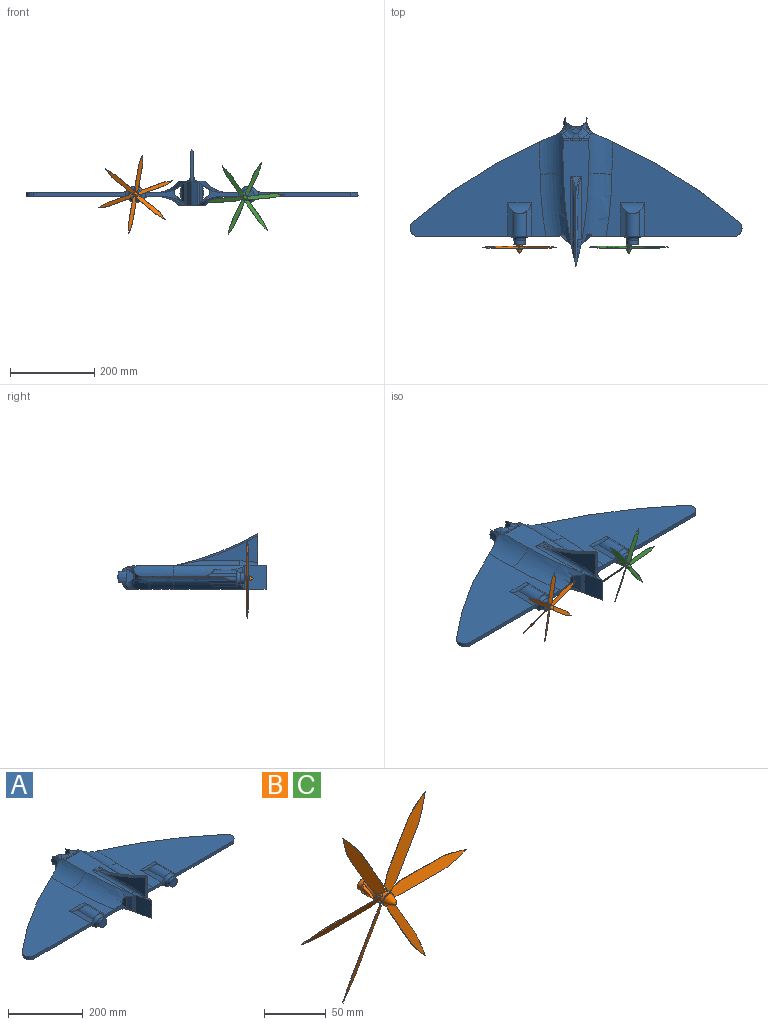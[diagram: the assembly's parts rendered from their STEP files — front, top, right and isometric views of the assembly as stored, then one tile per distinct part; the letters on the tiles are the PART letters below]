
ASSEMBLY  parts=3 mates=1
PART A: 103 faces, bbox 833.9x447.9x145.3 mm
  f0: plane 77.06x24.78mm, normal (0,-1,0), area 855.7mm2, adj f10,f21,f22,f28,f34,f40,f42,f43
  f1: plane 221.43x16.25mm, normal (0,-1,0), area 2215.1mm2, adj f2,f3,f14,f93,f95,f101
  f2: plane 321.92x225.03mm, normal (0,0,1), area 38652.2mm2, adj f1,f8,f12,f14,f31,f32,f91,f95
  f3: plane 323.52x206.51mm, normal (0,0,-1), area 32981mm2, adj f1,f8,f13,f14,f25,f26,f92,f93
  f4: plane 1.52x1.01mm, normal (0,0.71,-0.71), area 1mm2, adj f60,f77,f78
  f5: plane 19.73x12.89mm, normal (0,0.38,0.92), area 124.3mm2, adj f31,f63,f66,f72
  f6: plane 19.9x10.06mm, normal (0,0,1), area 101.6mm2, adj f15,f16,f44
  f7: plane 138.61x64.57mm, normal (-1,0,0), area 3823.6mm2, adj f44,f51,f52,f53
  f8: plane 77.03x24.74mm, normal (0,-1,0), area 855.7mm2, adj f2,f3,f11,f25,f32,f36,f37,f38
  f9: cylinder r=30mm len=39.86mm, axis (0,0,-1), area 421.5mm2, adj f12,f27,f31,f36,f37,f38,f63,f77
  f10: plane 57.68x24.14mm, normal (-0.63,-0.77,0), area 445.5mm2, adj f0,f16,f28,f34,f43,f57
  f11: plane 57.68x24.14mm, normal (0.63,-0.77,0), area 445.5mm2, adj f8,f15,f25,f32,f38,f58
  f12: cylinder r=1216.17mm len=343.76mm, axis (0,0,-1), area 1468.3mm2, adj f2,f9,f13,f14,f27,f31
  f13: torus R=1196.91mm, axis (0,0,-1), area 7777.9mm2, adj f3,f12,f14,f27
  f14: cylinder r=20.44mm len=31.58mm, axis (0,0,-1), area 312.3mm2, adj f1,f2,f3,f12,f13
  f15: cylinder r=891.18mm len=57mm, axis (0,0,1), area 2976.1mm2, adj f6,f11,f16,f17,f49,f50
  f16: cylinder r=891.18mm len=57mm, axis (0,0,1), area 2976.1mm2, adj f6,f10,f15,f17,f51
  f17: plane 330.75x64.66mm, normal (0,0,-1), area 14853.2mm2, adj f15,f16,f25,f26,f27,f28,f29,f30
  f18: plane 237.13x62.73mm, normal (0,0,1), area 8255mm2, adj f31,f32,f33,f34,f47,f48,f52,f55
  f19: cylinder r=20.44mm len=31.58mm, axis (0,0,-1), area 312.3mm2, adj f20,f21,f22,f23,f24
  f20: torus R=1196.91mm, axis (0,0,-1), area 7777.8mm2, adj f19,f21,f23,f30
  f21: plane 323.52x206.51mm, normal (0,0,-1), area 32981mm2, adj f0,f19,f20,f24,f28,f29,f83,f85
  f22: plane 321.92x225.03mm, normal (0,0,1), area 38652.2mm2, adj f0,f19,f23,f24,f33,f34,f84,f87
  f23: cylinder r=1216.17mm len=343.76mm, axis (0,0,-1), area 1468.3mm2, adj f19,f20,f22,f30,f33,f35
  f24: plane 221.43x16.25mm, normal (0,-1,0), area 2215.1mm2, adj f19,f21,f22,f86,f88,f102
  f25: torus R=940.17mm, axis (0,0,1), area 8346.4mm2, adj f3,f8,f11,f17,f26
  f26: torus R=810.61mm, axis (0,0,1), area 3113.6mm2, adj f3,f17,f25,f27
  f27: bspline ~70.07x54.57mm, area 1883.4mm2, adj f9,f12,f13,f17,f26,f77,f78
  f28: torus R=940.17mm, axis (0,0,1), area 8346.4mm2, adj f0,f10,f17,f21,f29
  f29: torus R=810.61mm, axis (0,0,1), area 3113.6mm2, adj f17,f21,f28,f30
  f30: bspline ~76.88x55.79mm, area 1883.5mm2, adj f17,f20,f23,f29,f35,f76,f80
  f31: torus R=816.85mm, axis (0,0,1), area 5583.6mm2, adj f2,f5,f9,f12,f18,f32,f63,f72
  f32: torus R=946.41mm, axis (0,0,1), area 9600.6mm2, adj f2,f8,f11,f18,f31,f36,f39,f49
  f33: torus R=816.85mm, axis (0,0,1), area 5583.6mm2, adj f18,f22,f23,f34,f35,f62,f64,f70
  f34: torus R=946.41mm, axis (0,0,1), area 9600.6mm2, adj f0,f10,f18,f22,f33,f41,f42,f51
  f35: cylinder r=30mm len=39.86mm, axis (0,0,1), area 421.5mm2, adj f23,f30,f33,f40,f42,f43,f64,f76
  f36: plane 256.61x17.38mm, normal (-0.57,0,-0.82), area 4867.7mm2, adj f8,f9,f32,f37,f39,f63,f65
  f37: plane 244.33x11.93mm, normal (-1,0,0), area 2914.8mm2, adj f8,f9,f36,f38
  f38: plane 285.27x26.63mm, normal (-0.62,0,0.79), area 5313.6mm2, adj f8,f9,f11,f37,f39,f58,f77
  f39: plane 286.48x42.71mm, normal (1,0,0), area 9851.4mm2, adj f32,f36,f38,f58,f59,f60,f65,f77
  f40: plane 244.33x11.93mm, normal (1,0,0), area 2914.8mm2, adj f0,f35,f42,f43
  f41: plane 286.48x42.71mm, normal (-1,0,0), area 9851.4mm2, adj f34,f42,f43,f57,f60,f61,f69,f76
  f42: plane 256.6x17.37mm, normal (0.57,0,-0.82), area 4867.7mm2, adj f0,f34,f35,f40,f41,f64,f69
  f43: plane 285.27x26.63mm, normal (0.62,0,0.79), area 5313.6mm2, adj f0,f10,f35,f40,f41,f57,f76
  f44: plane 74.53x10.63mm, normal (0,-1,0), area 543.5mm2, adj f6,f7,f45,f50,f51,f53,f54
  f45: plane 64.37x26.26mm, normal (1,-0.02,0), area 1436.2mm2, adj f44,f46,f49,f50,f54
  f46: plane 112.37x46.21mm, normal (1,0,0), area 2390.5mm2, adj f45,f48,f49,f54
  f47: cylinder r=820.16mm len=34.77mm, axis (-1,0,0), area 430.9mm2, adj f18,f55,f56
  f48: cylinder r=10mm len=148.7mm, axis (0,1,0), area 1925.9mm2, adj f18,f46,f49,f56
  f49: bspline ~28.84x11.57mm, area 220.2mm2, adj f15,f32,f45,f46,f48,f50
  f50: bspline ~35.02x9.75mm, area 256.1mm2, adj f15,f44,f45,f49
  f51: bspline ~48.75x10.78mm, area 465.3mm2, adj f7,f16,f34,f44,f52
  f52: cylinder r=10mm len=148.7mm, axis (0,-1,0), area 1925.9mm2, adj f7,f18,f51,f55
  f53: cone r=820.16mm half-angle=45deg, axis (-1,0,0), area 875.3mm2, adj f7,f44,f54,f55
  f54: cone r=820.16mm half-angle=45deg, axis (1,0,0), area 861.7mm2, adj f44,f45,f46,f53,f56
  f55: bspline ~53.44x16.63mm, area 248.7mm2, adj f18,f47,f52,f53,f56
  f56: bspline ~53.44x16.63mm, area 248.7mm2, adj f18,f47,f48,f54,f55
  f57: plane 46.27x16.35mm, normal (-0.9,-0.43,0), area 740.2mm2, adj f10,f34,f41,f43
  f58: plane 46.27x16.35mm, normal (0.9,-0.43,0), area 740.2mm2, adj f11,f32,f38,f39
  f59: cone r=28.26mm half-angle=70.4deg, axis (0,-1,0), area 0mm2, adj f39,f60
  f60: revolved ~127.16x57.17mm, area 13111.5mm2, adj f4,f39,f41,f59,f61,f65,f66,f67
  f61: cone r=28.26mm half-angle=70.4deg, axis (0,-1,0), area 0mm2, adj f41,f60
  f62: plane 19.73x12.89mm, normal (0,0.38,0.92), area 124.3mm2, adj f33,f64,f68,f70
  f63: bspline ~16.31x13.27mm, area 95.1mm2, adj f5,f9,f31,f36,f65
  f64: bspline ~16.31x13.27mm, area 95mm2, adj f33,f35,f42,f62,f69
  f65: bspline ~27.25x20.4mm, area 238.4mm2, adj f36,f39,f60,f63,f66
  f66: bspline ~31.61x29.28mm, area 377.4mm2, adj f5,f60,f65,f67,f74
  f67: bspline ~24.47x16.04mm, area 171.2mm2, adj f60,f66,f68,f73
  f68: bspline ~31.55x29.14mm, area 377.4mm2, adj f60,f62,f67,f69,f71
  f69: bspline ~27.25x20.4mm, area 238.4mm2, adj f41,f42,f60,f64,f68
  f70: cylinder r=10mm len=16.78mm, axis (1,0,0), area 65.1mm2, adj f18,f33,f62,f71
  f71: bspline ~9.1x4.14mm, area 19.5mm2, adj f18,f68,f70,f73
  f72: cylinder r=10mm len=16.78mm, axis (1,0,0), area 65.1mm2, adj f5,f18,f31,f74
  f73: bspline ~22.34x3.72mm, area 53mm2, adj f18,f67,f71,f74
  f74: bspline ~9.25x4.14mm, area 19.5mm2, adj f18,f66,f72,f73
  f75: plane 1.52x1.01mm, normal (0,0.71,-0.71), area 1mm2, adj f60,f76,f80
  f76: bspline ~21.99x17.11mm, area 161.1mm2, adj f30,f35,f41,f43,f60,f75,f80
  f77: bspline ~21.99x17.11mm, area 161.1mm2, adj f4,f9,f27,f38,f39,f60,f78
  f78: cylinder r=20mm len=14.14mm, axis (1,0,0), area 127.9mm2, adj f4,f17,f27,f77,f79
  f79: bspline ~40.21x15.34mm, area 292.9mm2, adj f17,f60,f78,f80
  f80: cylinder r=20mm len=14.14mm, axis (1,0,0), area 127.9mm2, adj f17,f30,f75,f76,f79
  f81: cylinder r=20mm len=62.57mm, axis (0,-1,0), area 2541mm2, adj f84,f87,f88,f102
  f82: cylinder r=20mm len=63.01mm, axis (0,-1,0), area 2482.1mm2, adj f83,f85,f86,f102
  f83: cylinder r=30mm len=54.36mm, axis (-1,0,0), area 1116.1mm2, adj f21,f82,f85,f86
  f84: cylinder r=30mm len=55.44mm, axis (1,0,0), area 1173.9mm2, adj f22,f81,f87,f88
  f85: plane 85.66x15.65mm, normal (0.47,0,-0.88), area 813.8mm2, adj f0,f21,f82,f83,f102
  f86: plane 85.66x15.65mm, normal (-0.47,0,-0.88), area 813.8mm2, adj f21,f24,f82,f83,f102
  f87: plane 85.75x15.95mm, normal (0.49,0,0.87), area 832.9mm2, adj f0,f22,f81,f84,f102
  f88: plane 85.75x15.95mm, normal (-0.49,0,0.87), area 832.9mm2, adj f22,f24,f81,f84,f102
  f89: cylinder r=20mm len=63.01mm, axis (0,-1,0), area 2482.1mm2, adj f92,f93,f94,f101
  f90: cylinder r=20mm len=62.57mm, axis (0,-1,0), area 2541mm2, adj f91,f95,f96,f101
  f91: cylinder r=30mm len=55.44mm, axis (1,0,0), area 1173.9mm2, adj f2,f90,f95,f96
  f92: cylinder r=30mm len=54.36mm, axis (-1,0,0), area 1116.1mm2, adj f3,f89,f93,f94
  f93: plane 85.66x15.65mm, normal (0.47,0,-0.88), area 813.8mm2, adj f1,f3,f89,f92,f101
  f94: plane 85.66x15.65mm, normal (-0.47,0,-0.88), area 813.8mm2, adj f3,f8,f89,f92,f101
  f95: plane 85.75x15.95mm, normal (0.49,0,0.87), area 832.9mm2, adj f1,f2,f90,f91,f101
  f96: plane 85.75x15.95mm, normal (-0.49,0,0.87), area 832.9mm2, adj f2,f8,f90,f91,f101
  f97: cylinder r=13.21mm len=26.42mm, axis (0,1,0), area 829.9mm2, adj f98,f102
  f98: plane 26.42x26.42mm, normal (0,-1,0), area 548mm2, adj f97
  f99: cylinder r=13.21mm len=26.42mm, axis (0,1,0), area 829.9mm2, adj f100,f101
  f100: plane 26.42x26.42mm, normal (0,-1,0), area 548mm2, adj f99
  f101: torus R=23.21mm, axis (0,-1,0), area 1349.4mm2, adj f1,f8,f89,f90,f93,f94,f95,f96
  f102: torus R=23.21mm, axis (0,-1,0), area 1349.4mm2, adj f0,f24,f81,f82,f85,f86,f87,f88
PART B: 111 faces, bbox 187.8x39.9x162.9 mm
  f0: cylinder r=6mm len=21.6mm, axis (0,-1,0), area 67.9mm2, adj f4,f8,f15,f17,f92,f100,f101,f105
  f1: cylinder r=6mm len=25mm, axis (0,-1,0), area 318.8mm2, adj f2,f9,f24,f35,f43,f44,f46,f47
  f2: cylinder r=6mm len=2.22mm, axis (0,-1,0), area 1.5mm2, adj f1,f61,f102
  f3: plane 42.83x24.85mm, normal (0.76,0.49,0.44), area 25.2mm2, adj f4,f99,f101,f108
  f4: plane 77.51x47.04mm, normal (-0.38,0.9,-0.22), area 765.3mm2, adj f0,f3,f12,f101,f105,f108,f109
  f5: cylinder r=6mm len=21.6mm, axis (0,-1,0), area 67.5mm2, adj f6,f7,f10,f16,f23,f27,f29,f85
  f6: plane 0.59x0.28mm, normal (-0.38,0.9,0.22), area 0.1mm2, adj f5,f10,f105
  f7: plane 78.42x44.94mm, normal (-0.38,0.9,0.22), area 760.3mm2, adj f5,f11,f18,f19,f94,f97,f98,f104
  f8: plane 0.53x0.25mm, normal (0.38,-0.9,-0.22), area 0.1mm2, adj f0,f10,f105
  f9: plane 78.29x44.97mm, normal (0.38,-0.9,-0.22), area 762mm2, adj f1,f11,f18,f19,f94,f97,f98,f104
  f10: cylinder r=169.83mm len=12.1mm, axis (0.38,-0.9,-0.22), area 15.1mm2, adj f5,f6,f8,f16,f28,f29,f92,f105
  f11: cylinder r=169.83mm len=11.51mm, axis (0.38,-0.9,-0.22), area 6.2mm2, adj f7,f9,f19,f104
  f12: plane 43.98x25.52mm, normal (-0.78,-0.44,-0.45), area 25.9mm2, adj f4,f99,f105,f109
  f13: cylinder r=5mm len=10mm, axis (0,1,0), area 151.9mm2, adj f14,f15,f16,f17,f27,f29,f39,f40
  f14: cylinder r=5mm len=1.5mm, axis (0,1,0), area 0.7mm2, adj f13,f28,f39
  f15: plane 4.8x2.98mm, normal (0,1,0), area 4.5mm2, adj f0,f13,f17,f100
  f16: cylinder r=5.1mm len=21.2mm, axis (0.38,-0.9,-0.22), area 88.2mm2, adj f5,f10,f13,f17,f27,f28,f29,f92
  f17: plane 19.81x9.22mm, normal (-0.78,-0.44,0.45), area 83mm2, adj f0,f13,f15,f16,f92,f100,f101
  f18: plane 43.98x25.52mm, normal (-0.78,-0.44,0.45), area 25.9mm2, adj f7,f9,f94,f98
  f19: plane 42.83x24.85mm, normal (0.76,0.49,-0.44), area 25.2mm2, adj f7,f9,f11,f97
  f20: cylinder r=6mm len=21.6mm, axis (0,-1,0), area 67.5mm2, adj f21,f22,f25,f28,f34,f39,f41,f78
  f21: plane 0.55x0.39mm, normal (0,0.9,0.44), area 0.1mm2, adj f20,f25,f94
  f22: plane 88.81x9.34mm, normal (0,0.9,0.44), area 760.3mm2, adj f20,f26,f30,f38,f87,f90,f91,f93
  f23: plane 0.5x0.34mm, normal (0,-0.9,-0.44), area 0.1mm2, adj f5,f25,f94
  f24: plane 88.66x9.34mm, normal (0,-0.9,-0.44), area 762mm2, adj f1,f26,f30,f38,f87,f90,f91,f93
  f25: cylinder r=169.83mm len=12.1mm, axis (0,-0.9,-0.44), area 15.1mm2, adj f20,f21,f23,f28,f40,f41,f85,f94
  f26: cylinder r=169.83mm len=12.02mm, axis (0,-0.9,-0.44), area 6.2mm2, adj f22,f24,f30,f93
  f27: plane 4.2x3.13mm, normal (0,1,0), area 4.5mm2, adj f5,f13,f16,f29
  f28: cylinder r=5.1mm len=21.2mm, axis (0,-0.9,-0.44), area 88.2mm2, adj f10,f14,f16,f20,f25,f29,f39,f40
  f29: plane 19.81x9.62mm, normal (0,-0.44,0.9), area 83mm2, adj f5,f10,f13,f16,f27,f28,f85
  f30: plane 49.46x0.45mm, normal (0,0.49,-0.87), area 25.2mm2, adj f22,f24,f26,f90
  f31: cylinder r=6mm len=21.6mm, axis (0,-1,0), area 67.5mm2, adj f32,f33,f36,f40,f45,f50,f52,f71
  f32: plane 0.57x0.42mm, normal (0.38,0.9,0.22), area 0.1mm2, adj f31,f36,f87
  f33: plane 76.48x47.03mm, normal (0.38,0.9,0.22), area 760.3mm2, adj f31,f37,f42,f49,f80,f83,f84,f86
  f34: plane 0.5x0.38mm, normal (-0.38,-0.9,-0.22), area 0.1mm2, adj f20,f36,f87
  f35: plane 75.86x46.95mm, normal (-0.38,-0.9,-0.22), area 762mm2, adj f1,f37,f42,f49,f80,f83,f84,f86
  f36: cylinder r=169.83mm len=12.1mm, axis (-0.38,-0.9,-0.22), area 15.1mm2, adj f31,f32,f34,f40,f51,f52,f78,f87
  f37: cylinder r=169.83mm len=9.53mm, axis (-0.38,-0.9,-0.22), area 6.2mm2, adj f33,f35,f42,f86
  f38: plane 50.65x0.46mm, normal (0,-0.44,0.9), area 25.9mm2, adj f22,f24,f87,f91
  f39: plane 5.19x1.54mm, normal (0,1,0), area 4.5mm2, adj f13,f14,f20,f28,f41
  f40: cylinder r=5.1mm len=21.2mm, axis (-0.38,-0.9,-0.22), area 88.2mm2, adj f13,f25,f28,f31,f36,f41,f50,f51
  f41: plane 19.81x9.44mm, normal (0.78,-0.44,0.45), area 83mm2, adj f13,f20,f25,f28,f39,f40,f78
  f42: plane 42.83x24.85mm, normal (-0.76,0.49,-0.44), area 25.2mm2, adj f33,f35,f37,f83
  f43: plane 0.59x0.28mm, normal (0.38,0.9,-0.22), area 0.1mm2, adj f1,f47,f80
  f44: plane 78.4x44.92mm, normal (0.38,0.9,-0.22), area 760.3mm2, adj f1,f48,f53,f54,f73,f76,f77,f79
  f45: plane 0.53x0.25mm, normal (-0.38,-0.9,0.22), area 0.1mm2, adj f31,f47,f80
  f46: plane 78.29x44.97mm, normal (-0.38,-0.9,0.22), area 762mm2, adj f1,f48,f53,f54,f73,f76,f77,f79
  f47: cylinder r=169.83mm len=12.1mm, axis (-0.38,-0.9,0.22), area 15.1mm2, adj f1,f43,f45,f51,f71,f80
  f48: cylinder r=169.83mm len=11.51mm, axis (-0.38,-0.9,0.22), area 6.2mm2, adj f44,f46,f54,f79
  f49: plane 43.98x25.52mm, normal (0.78,-0.44,0.45), area 25.9mm2, adj f33,f35,f80,f84
  f50: plane 4.8x2.98mm, normal (0,1,0), area 4.5mm2, adj f13,f31,f40,f52
  f51: cylinder r=5.1mm len=21.2mm, axis (-0.38,-0.9,0.22), area 88.2mm2, adj f1,f13,f36,f40,f47,f52,f61,f71
  f52: plane 19.81x9.22mm, normal (0.78,-0.44,-0.45), area 83mm2, adj f13,f31,f36,f40,f50,f51,f71
  f53: plane 43.98x25.52mm, normal (0.78,-0.44,-0.45), area 25.9mm2, adj f44,f46,f73,f77
  f54: plane 42.83x24.85mm, normal (-0.76,0.49,0.44), area 25.2mm2, adj f44,f46,f48,f76
  f55: plane 0.55x0.39mm, normal (0,0.9,-0.44), area 0.1mm2, adj f1,f59,f73
  f56: plane 88.79x9.32mm, normal (0,0.9,-0.44), area 760.3mm2, adj f1,f60,f62,f63,f64,f65,f66,f72
  f57: plane 0.5x0.34mm, normal (0,-0.9,0.44), area 0.1mm2, adj f1,f59,f73
  f58: plane 88.66x9.34mm, normal (0,-0.9,0.44), area 762mm2, adj f1,f60,f62,f63,f64,f65,f66,f72
  f59: cylinder r=169.83mm len=0.62mm, axis (0,-0.9,0.44), area 0.3mm2, adj f1,f55,f57,f73
  f60: cylinder r=169.83mm len=12.02mm, axis (0,-0.9,0.44), area 6.2mm2, adj f56,f58,f63,f72
  f61: plane 8.11x6.12mm, normal (0,1,0), area 10.6mm2, adj f1,f2,f13,f51,f68,f69,f102
  f62: plane 50.65x0.46mm, normal (0,-0.44,-0.9), area 25.9mm2, adj f56,f58,f65,f66
  f63: plane 49.46x0.45mm, normal (0,0.49,0.87), area 25.2mm2, adj f56,f58,f60,f64
  f64: cylinder r=169.83mm len=23.95mm, axis (0,-0.9,0.44), area 12.5mm2, adj f56,f58,f63,f65
  f65: cylinder r=208.02mm len=26.64mm, axis (0,-0.9,0.44), area 13.9mm2, adj f56,f58,f62,f64
  f66: cylinder r=208.02mm len=11.45mm, axis (0,-0.9,0.44), area 5.9mm2, adj f1,f56,f58,f62
  f67: plane 10x10mm, normal (0,1,0), area 78.5mm2, adj f13
  f68: cylinder r=5.1mm len=1.66mm, axis (0,-0.9,0.44), area 0.8mm2, adj f13,f61,f69
  f69: plane 1.53x1.5mm, normal (0,-0.44,-0.9), area 1.5mm2, adj f13,f61,f68
  f70: plane 12x12mm, normal (0,-1,0), area 35.9mm2, adj f1,f110
  f71: plane 4.54x2.55mm, normal (0.38,0.9,-0.22), area 4.2mm2, adj f31,f47,f51,f52
  f72: plane 4.03x3.97mm, normal (-0.78,0.44,0.45), area 5mm2, adj f1,f56,f58,f60,f74,f75
  f73: cylinder r=208.02mm len=10.66mm, axis (-0.38,-0.9,0.22), area 8.3mm2, adj f1,f44,f46,f53,f55,f57,f59,f74
  f74: cylinder r=4.82mm len=4.02mm, axis (-0.38,-0.9,0.22), area 8.1mm2, adj f1,f56,f72,f73,f75
  f75: plane 3.43x1.44mm, normal (0.38,0.9,-0.22), area 2.5mm2, adj f1,f72,f73,f74
  f76: cylinder r=169.83mm len=18.48mm, axis (-0.38,-0.9,0.22), area 12.5mm2, adj f44,f46,f54,f77
  f77: cylinder r=208.02mm len=25.45mm, axis (-0.38,-0.9,0.22), area 13.9mm2, adj f44,f46,f53,f76
  f78: plane 5.12x2.11mm, normal (0.38,0.9,0.22), area 4.2mm2, adj f20,f36,f40,f41
  f79: plane 4.93x4.03mm, normal (-0.78,0.44,-0.45), area 5mm2, adj f1,f44,f46,f48,f81,f82
  f80: cylinder r=208.02mm len=12.37mm, axis (-0.38,-0.9,-0.22), area 8.3mm2, adj f1,f31,f33,f35,f43,f45,f47,f49
  f81: cylinder r=4.82mm len=4.02mm, axis (-0.38,-0.9,-0.22), area 8.1mm2, adj f1,f44,f79,f80,f82
  f82: plane 2.89x1.89mm, normal (0.38,0.9,0.22), area 2.5mm2, adj f1,f79,f80,f81
  f83: cylinder r=169.83mm len=23.23mm, axis (-0.38,-0.9,-0.22), area 12.5mm2, adj f33,f35,f42,f84
  f84: cylinder r=208.02mm len=20.91mm, axis (-0.38,-0.9,-0.22), area 13.9mm2, adj f33,f35,f49,f83
  f85: plane 4.37x3mm, normal (0,0.9,0.44), area 4.2mm2, adj f5,f25,f28,f29
  f86: plane 4.65x4.03mm, normal (0,0.44,-0.9), area 5mm2, adj f1,f33,f35,f37,f88,f89
  f87: cylinder r=208.02mm len=12.4mm, axis (0,-0.9,-0.44), area 8.3mm2, adj f20,f22,f24,f31,f32,f34,f36,f38
  f88: cylinder r=4.82mm len=4.02mm, axis (0,-0.9,-0.44), area 8.1mm2, adj f31,f33,f86,f87,f89
  f89: plane 3.07x1.76mm, normal (0,0.9,0.44), area 2.5mm2, adj f1,f86,f87,f88
  f90: cylinder r=169.83mm len=23.95mm, axis (0,-0.9,-0.44), area 12.5mm2, adj f22,f24,f30,f91
  f91: cylinder r=208.02mm len=26.64mm, axis (0,-0.9,-0.44), area 13.9mm2, adj f22,f24,f38,f90
  f92: plane 4.54x2.55mm, normal (-0.38,0.9,0.22), area 4.2mm2, adj f0,f10,f16,f17
  f93: plane 4.03x3.97mm, normal (0.78,0.44,-0.45), area 5mm2, adj f1,f22,f24,f26,f95,f96
  f94: cylinder r=208.02mm len=10.66mm, axis (0.38,-0.9,-0.22), area 8.3mm2, adj f5,f7,f9,f18,f20,f21,f23,f25
  f95: cylinder r=4.82mm len=4.02mm, axis (0.38,-0.9,-0.22), area 8.1mm2, adj f20,f22,f93,f94,f96
  f96: plane 3.43x1.44mm, normal (-0.38,0.9,0.22), area 2.5mm2, adj f1,f93,f94,f95
  f97: cylinder r=169.83mm len=18.48mm, axis (0.38,-0.9,-0.22), area 12.5mm2, adj f7,f9,f19,f98
  f98: cylinder r=208.02mm len=25.45mm, axis (0.38,-0.9,-0.22), area 13.9mm2, adj f7,f9,f18,f97
  f99: plane 77.55x46.97mm, normal (0.38,-0.9,0.22), area 766.6mm2, adj f1,f3,f12,f101,f105,f108,f109
  f100: cylinder r=5.1mm len=21.2mm, axis (0.38,-0.9,0.22), area 88.2mm2, adj f0,f13,f15,f16,f17,f101,f102,f103
  f101: cylinder r=169.83mm len=15.61mm, axis (0.38,-0.9,0.22), area 22.7mm2, adj f0,f3,f4,f16,f17,f99,f100,f103
  f102: plane 19.9x9.53mm, normal (-0.78,-0.44,-0.45), area 83.1mm2, adj f1,f2,f13,f61,f100,f103
  f103: plane 4.99x1.97mm, normal (-0.38,0.9,-0.22), area 4.2mm2, adj f1,f100,f101,f102
  f104: plane 4.93x4.03mm, normal (0.78,0.44,0.45), area 5mm2, adj f1,f7,f9,f11,f106,f107
  f105: cylinder r=208.02mm len=12.37mm, axis (0.38,-0.9,0.22), area 8.3mm2, adj f0,f4,f5,f6,f8,f10,f12,f99
  f106: cylinder r=4.82mm len=4.02mm, axis (0.38,-0.9,0.22), area 8.1mm2, adj f5,f7,f104,f105,f107
  f107: plane 2.89x1.89mm, normal (-0.38,0.9,-0.22), area 2.5mm2, adj f1,f104,f105,f106
  f108: cylinder r=169.83mm len=23.23mm, axis (0.38,-0.9,0.22), area 12.5mm2, adj f3,f4,f99,f109
  f109: cylinder r=208.02mm len=20.91mm, axis (0.38,-0.9,0.22), area 13.9mm2, adj f4,f12,f99,f108
  f110: revolved ~9.91x9.91mm, area 214.4mm2, adj f70
PART C: same geometry as B
PLACE A t=(-85.15,77.71,-104.78)mm
PLACE B rot(axis=(0,-1,0),20deg) t=(-194.04,-38.73,-99.36)mm
PLACE C rot(axis=(0,1,0),175deg) t=(65.04,-38.2,-108.28)mm
MATE revolute A.f81 <-> B.f13  axis (0,-1,0) through (-194.04,-38.73,-99.36)mm
